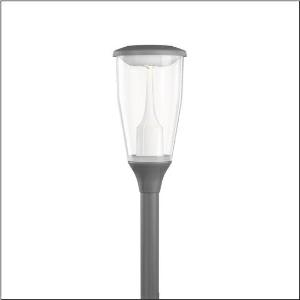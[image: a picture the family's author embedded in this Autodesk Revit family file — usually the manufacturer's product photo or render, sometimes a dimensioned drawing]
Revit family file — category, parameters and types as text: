
# Revit family: dl_11_iq___p1_0a_5xa5575ff14h000022_b904
name_source: partatom
category: Lighting Fixtures
units: mm (PartAtom-declared; Revit-internal decimal feet)

## family parameters
Cut with Voids When Loaded = No
Host = Face
Light Source = No
Part Type = Normal
Room Calculation Point = No
Round Connector Dimension = Use Diameter
Shared = No

## types (1)
- --- (1 x LED, 1530 lm, 10.5 W, 3000K)
    Apparent Load = 11 VA
    CIE Flux Codes = 34 63 91 95 100
    Color Rendering = 70
    Color Temperature = 3000K
    Default Elevation = 1800 mm
    Description = DL 11 iQ, mast luminaire, Module 540 iQ-SR, primary light control with 3 zone facetted reflector, of plastic, silver coated, highly specular, structured, primary optical cover: cover, of PMMA, transparent, light distribution: P1.0a, light emission: direct distribution, primary light characteristic: asymmetric, installation type: post-top, LED, High Power LED, rated luminous flux: 1.560lm, luminous efficacy: 149lm/W, light colour: 730, colour temperature: 3000K, control: Street-Remote, Auto-Match, Temp-Guard, Lumen-Switch, Night-Set, Smart-Wire, Light-Fading, Desk-Remote (wireless, voltage-free reading and setting of iQ features in the workshop via application-optimized NFC function/RFID function), optimised constant luminous flux control (CLO 2.0), mains connection: 220..240V, AC, 50/60Hz, connection cable pre-assembled, cable length: 5,5m, wiring characteristics: H07RN-F, 5-core, 1.5mm², start of lifetime: 10W, end of service life: 11W, reduction: 5W, luminaire housing, upper part, of diecast aluminium, coated, Siteco® metallic grey (DB 702S), spigot size: 76mm (post-top), post-top mast mounting element, of diecast aluminium, coated, Siteco® metallic grey (DB 702S), Module 540 iQ-SR, traffic white (RAL 9016), equipment: standard, protection rating (complete): IP66, insulation class (complete): insulation class II (safety insulation), certification: CE, ENEC, ENEC+, VDE, packaging unit: 1 piece

Light Distribution: P1.0a
    Height = 665 mm
    Lamp = 1 x LED
    Lamp Light Flux = 1530 lm
    Lamp Power = 10.5 W
    Lamp count = 1
    Length = 334 mm
    Luminous efficacy = 146 lm/W
    Manufacturer = Siteco
    ModVariant = No
    Model = 5XA5575FF14H000022
    Number of Poles = 1
    OnlyDefault = Yes
    Power Factor = 1
    Product Name = DL 11 iQ | P1.0a
    Product group = mast luminaire | pylon top
    ProductGroupID = 6100
    Protection Class = Protection class II
    Protection Degree = IP 66
    RLX_Detail_Level = 1
    RLX_Emergency_Light_Flux = 0 lm
    RLX_Emergency_Type = 0
    RLX_Emergency_Type_DB = No
    RlxData = <blob elided: 104301 chars, md5=a75782e7>
    Socket = socket
    Standby Power = 0 W
    System Light Flux = 1530 lm
    System Power = 11 W
    Type Comments = factory setting: luminous flux: 100 % | dim-lin: 254 | 419 mA
    Type Image = l_1258354.jpg
    URL = http://relux.com
    VarID = @adj_024149
    Voltage = 0 V
    Weight = 0.00 kg
    Width = 0 mm  [stored 0 ft]

note: [stored X ft] marks values corroborated as IEEE doubles in the binary element streams (Revit-internal decimal feet)

## geometry (parser evidence)
native form markers: Blend x4, Sweep x12
no freeform markers — native parametric forms only
